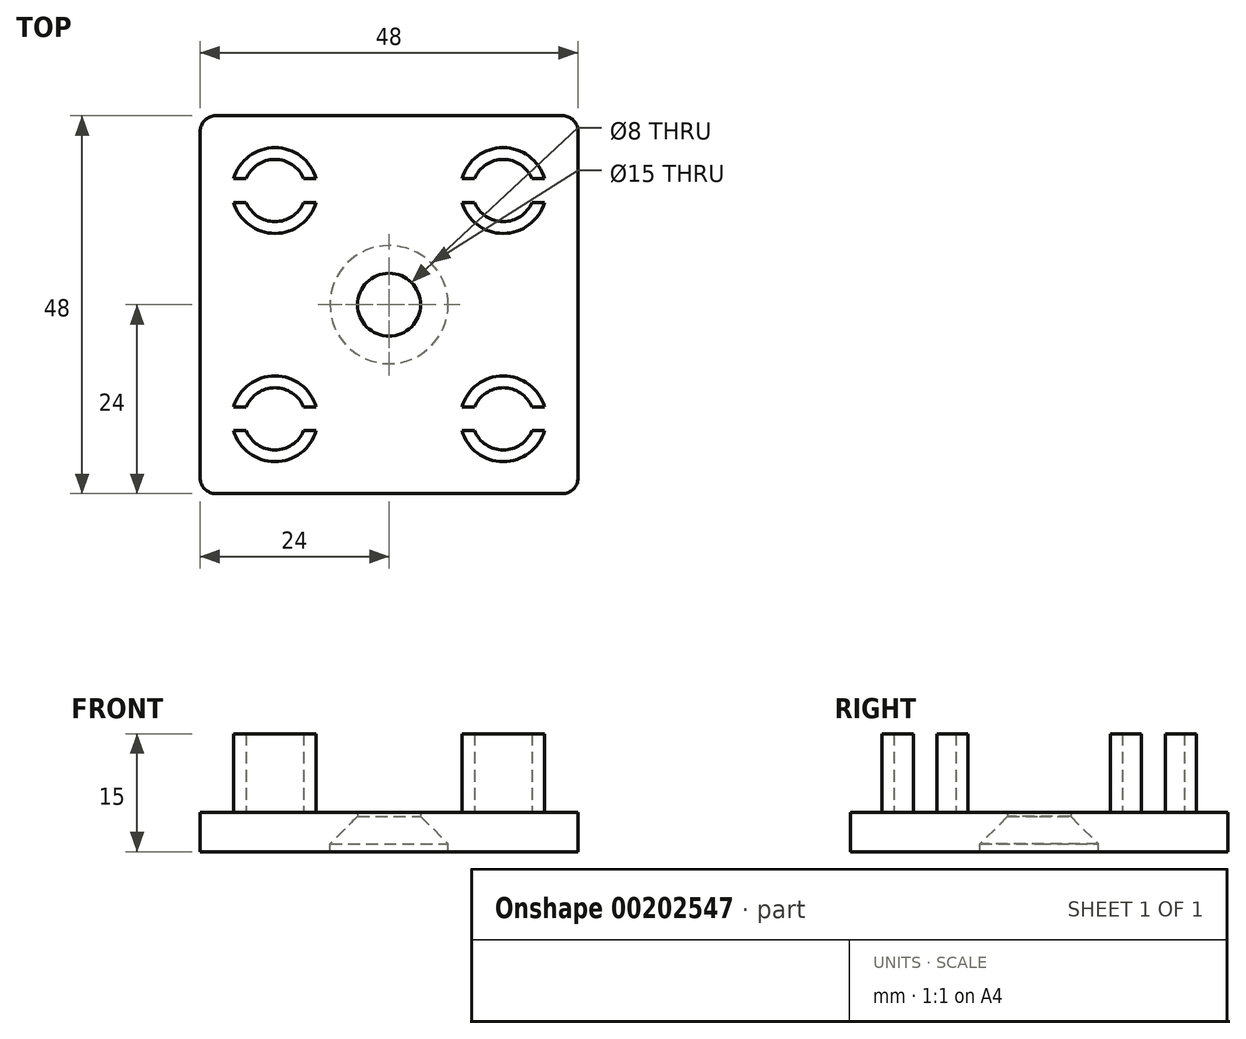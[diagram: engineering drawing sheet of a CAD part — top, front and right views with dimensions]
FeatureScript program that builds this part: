
annotation { "Feature Type Name" : "Feature", "Feature Type Description" : "" }
export const myFeature = defineFeature(function(context is Context, id is Id, definition is map)
    precondition{}
    {
        {
            var Q0;
            Q0=qCreatedBy(makeId("Top.planeOp"),FACE);
            var sketch = newSketch(context, id + "F0", { "sketchPlane" : qUnion([Q0])});
            skLineSegment(sketch, "E0.bottom", {"start": v(22, 24) * mm, "end": v(-22, 24) * mm});
            skLineSegment(sketch, "E0.top", {"start": v(22, -24) * mm, "end": v(-22, -24) * mm});
            skLineSegment(sketch, "E0.left", {"start": v(24, 22) * mm, "end": v(24, -22) * mm});
            skLineSegment(sketch, "E0.right", {"start": v(-24, 22) * mm, "end": v(-24, -22) * mm});
            skPoint(sketch, "E0.middle", {"position": v(0, 0) * mm});
            skPoint(sketch, "E1.visualSharp", {"position": v(-24, 24) * mm});
            skArc(sketch, "E1.filletArc", {"start": v(-22, 24) * mm, "mid": v(-23.41, 23.41) * mm, "end": v(-24, 22) * mm});
            skPoint(sketch, "E2.visualSharp", {"position": v(24, 24) * mm});
            skArc(sketch, "E2.filletArc", {"start": v(24, 22) * mm, "mid": v(23.41, 23.41) * mm, "end": v(22, 24) * mm});
            skPoint(sketch, "E3.visualSharp", {"position": v(24, -24) * mm});
            skArc(sketch, "E3.filletArc", {"start": v(22, -24) * mm, "mid": v(23.41, -23.41) * mm, "end": v(24, -22) * mm});
            skPoint(sketch, "E4.visualSharp", {"position": v(-24, -24) * mm});
            skArc(sketch, "E4.filletArc", {"start": v(-24, -22) * mm, "mid": v(-23.41, -23.41) * mm, "end": v(-22, -24) * mm});
            skLineSegment(sketch, "E5.0", {"start": v(18, 18) * mm, "end": v(-18, 18) * mm});
            skLineSegment(sketch, "E5.1", {"start": v(18, 18) * mm, "end": v(18, -18) * mm});
            skLineSegment(sketch, "E5.2", {"start": v(18, -18) * mm, "end": v(-18, -18) * mm});
            skLineSegment(sketch, "E5.3", {"start": v(-18, 18) * mm, "end": v(-18, -18) * mm});
            skSolve(sketch);
        }
        {
            var Q0;
            Q0=makeQuery(id+"F0.imprint","IMPRINT",FACE,{"disambiguationData":[TD([[makeQuery(id+"F0.imprint","IMPRINT",EDGE,{"derivedFrom":sQuery(id+"F0.wireOp",EDGE,"E0.bottom")}),1.0]])]});
            var Q1;
            Q1=makeQuery(id+"F0.imprint","IMPRINT",FACE,{"disambiguationData":[TD([[makeQuery(id+"F0.imprint","IMPRINT",EDGE,{"derivedFrom":sQuery(id+"F0.wireOp",EDGE,"E5.0")}),1.0]])]});
            extrude(context, id + "F1", {"entities" : qUnion([Q0, Q1]), "oppositeDirection" : true, "depth" : 4 * mm});
        }
        {
            var Q0;
            Q0=makeQuery(id+"F1.opExtrude","CAP_FACE",FACE,{"disambiguationData":[OSD([sQuery(id+"F0.wireOp",EDGE,"E0.bottom"),sQuery(id+"F0.wireOp",EDGE,"E0.top"),sQuery(id+"F0.wireOp",EDGE,"E0.left"),sQuery(id+"F0.wireOp",EDGE,"E0.right"),sQuery(id+"F0.wireOp",EDGE,"E1.filletArc"),sQuery(id+"F0.wireOp",EDGE,"E2.filletArc"),sQuery(id+"F0.wireOp",EDGE,"E3.filletArc"),sQuery(id+"F0.wireOp",EDGE,"E4.filletArc")])],"isStart":true});
            var sketch = newSketch(context, id + "F2", { "sketchPlane" : qUnion([Q0])});
            skLineSegment(sketch, "E6.0", {"start": v(20, 20) * mm, "end": v(-20, 20) * mm});
            skLineSegment(sketch, "E6.1", {"start": v(20, 20) * mm, "end": v(20, -20) * mm});
            skLineSegment(sketch, "E6.2", {"start": v(20, -20) * mm, "end": v(-20, -20) * mm});
            skLineSegment(sketch, "E6.3", {"start": v(-20, 20) * mm, "end": v(-20, -20) * mm});
            skCircle(sketch, "E7", {"center": v(0, 0) * mm, "radius": 3.75 * mm});
            skLineSegment(sketch, "E8.bottom", {"start": v(-20, 20) * mm, "end": v(-9, 20) * mm});
            skLineSegment(sketch, "E8.top", {"start": v(-20, 9) * mm, "end": v(-9, 9) * mm});
            skLineSegment(sketch, "E8.left", {"start": v(-20, 20) * mm, "end": v(-20, 9) * mm});
            skLineSegment(sketch, "E8.right", {"start": v(-9, 20) * mm, "end": v(-9, 9) * mm});
            skLineSegment(sketch, "E9.bottom", {"start": v(20, 20) * mm, "end": v(9, 20) * mm});
            skLineSegment(sketch, "E9.top", {"start": v(20, 9) * mm, "end": v(9, 9) * mm});
            skLineSegment(sketch, "E9.left", {"start": v(20, 20) * mm, "end": v(20, 9) * mm});
            skLineSegment(sketch, "E9.right", {"start": v(9, 20) * mm, "end": v(9, 9) * mm});
            skLineSegment(sketch, "E10.bottom", {"start": v(20, -20) * mm, "end": v(9, -20) * mm});
            skLineSegment(sketch, "E10.top", {"start": v(20, -9) * mm, "end": v(9, -9) * mm});
            skLineSegment(sketch, "E10.left", {"start": v(20, -20) * mm, "end": v(20, -9) * mm});
            skLineSegment(sketch, "E10.right", {"start": v(9, -20) * mm, "end": v(9, -9) * mm});
            skLineSegment(sketch, "E11.bottom", {"start": v(-20, -20) * mm, "end": v(-9, -20) * mm});
            skLineSegment(sketch, "E11.top", {"start": v(-20, -9) * mm, "end": v(-9, -9) * mm});
            skLineSegment(sketch, "E11.left", {"start": v(-20, -20) * mm, "end": v(-20, -9) * mm});
            skLineSegment(sketch, "E11.right", {"start": v(-9, -20) * mm, "end": v(-9, -9) * mm});
            skCircle(sketch, "E12", {"center": v(14.5, 14.5) * mm, "radius": 5.45 * mm});
            skPoint(sketch, "E12.centerSnap0", {"position": v(20, 14.5) * mm});
            skPoint(sketch, "E12.centerSnap1", {"position": v(14.5, 20) * mm});
            skCircle(sketch, "E13", {"center": v(-14.5, 14.5) * mm, "radius": 5.45 * mm});
            skPoint(sketch, "E13.centerSnap0", {"position": v(-14.5, 20) * mm});
            skPoint(sketch, "E13.centerSnap1", {"position": v(-9, 14.5) * mm});
            skCircle(sketch, "E14", {"center": v(-14.5, -14.5) * mm, "radius": 5.45 * mm});
            skPoint(sketch, "E14.centerSnap0", {"position": v(-14.5, -9) * mm});
            skPoint(sketch, "E14.centerSnap1", {"position": v(-9, -14.5) * mm});
            skCircle(sketch, "E15", {"center": v(14.5, -14.5) * mm, "radius": 5.45 * mm});
            skPoint(sketch, "E15.centerSnap0", {"position": v(14.5, -9) * mm});
            skPoint(sketch, "E15.centerSnap1", {"position": v(20, -14.5) * mm});
            skCircle(sketch, "E16", {"center": v(14.5, 14.5) * mm, "radius": 3.95 * mm});
            skCircle(sketch, "E17", {"center": v(14.5, -14.5) * mm, "radius": 3.95 * mm});
            skCircle(sketch, "E18", {"center": v(-14.5, -14.5) * mm, "radius": 3.95 * mm});
            skCircle(sketch, "E19", {"center": v(-14.5, 14.5) * mm, "radius": 3.95 * mm});
            skLineSegment(sketch, "E20.bottom", {"start": v(-9, 16) * mm, "end": v(-20, 16) * mm});
            skLineSegment(sketch, "E20.top", {"start": v(-9, 13) * mm, "end": v(-20, 13) * mm});
            skLineSegment(sketch, "E20.left", {"start": v(-9, 16) * mm, "end": v(-9, 13) * mm});
            skLineSegment(sketch, "E20.right", {"start": v(-20, 16) * mm, "end": v(-20, 13) * mm});
            skLineSegment(sketch, "E21.bottom", {"start": v(9, 16) * mm, "end": v(20, 16) * mm});
            skLineSegment(sketch, "E21.top", {"start": v(9, 13) * mm, "end": v(20, 13) * mm});
            skLineSegment(sketch, "E21.left", {"start": v(9, 16) * mm, "end": v(9, 13) * mm});
            skLineSegment(sketch, "E21.right", {"start": v(20, 16) * mm, "end": v(20, 13) * mm});
            skLineSegment(sketch, "E22.bottom", {"start": v(9, -13) * mm, "end": v(20, -13) * mm});
            skLineSegment(sketch, "E22.top", {"start": v(9, -16) * mm, "end": v(20, -16) * mm});
            skLineSegment(sketch, "E22.left", {"start": v(9, -13) * mm, "end": v(9, -16) * mm});
            skLineSegment(sketch, "E22.right", {"start": v(20, -13) * mm, "end": v(20, -16) * mm});
            skLineSegment(sketch, "E23.bottom", {"start": v(-9, -13) * mm, "end": v(-20, -13) * mm});
            skLineSegment(sketch, "E23.top", {"start": v(-9, -16) * mm, "end": v(-20, -16) * mm});
            skLineSegment(sketch, "E23.left", {"start": v(-9, -13) * mm, "end": v(-9, -16) * mm});
            skLineSegment(sketch, "E23.right", {"start": v(-20, -13) * mm, "end": v(-20, -16) * mm});
            skSolve(sketch);
        }
        {
            var Q0;
            {var subQ0=sQuery(id+"F2.wireOp",EDGE,"E20.bottom");var subQ1=sQuery(id+"F2.wireOp",EDGE,"E13");var subQ2=makeQuery(id+"F2.imprint","INTERSECT",VERTEX,{"disambiguationData":[OD(0.0)],"derivedFrom":[subQ1,subQ0]});Q0=makeQuery(id+"F2.imprint","IMPRINT",FACE,{"disambiguationData":[TD([[makeQuery(id+"F2.imprint","IMPRINT",EDGE,{"disambiguationData":[TD([[subQ2,1.0]])],"derivedFrom":subQ1}),1.0]])]});}
            var Q1;
            {var subQ0=sQuery(id+"F2.wireOp",EDGE,"E20.top");var subQ1=sQuery(id+"F2.wireOp",EDGE,"E13");var subQ2=makeQuery(id+"F2.imprint","INTERSECT",VERTEX,{"disambiguationData":[OD(0.0)],"derivedFrom":[subQ1,subQ0]});Q1=makeQuery(id+"F2.imprint","IMPRINT",FACE,{"disambiguationData":[TD([[makeQuery(id+"F2.imprint","IMPRINT",EDGE,{"disambiguationData":[TD([[subQ2,-1.0]])],"derivedFrom":subQ1}),1.0]])]});}
            var Q2;
            {var subQ0=sQuery(id+"F2.wireOp",EDGE,"E21.bottom");var subQ1=sQuery(id+"F2.wireOp",EDGE,"E12");var subQ2=makeQuery(id+"F2.imprint","INTERSECT",VERTEX,{"disambiguationData":[OD(0.0)],"derivedFrom":[subQ1,subQ0]});Q2=makeQuery(id+"F2.imprint","IMPRINT",FACE,{"disambiguationData":[TD([[makeQuery(id+"F2.imprint","IMPRINT",EDGE,{"disambiguationData":[TD([[subQ2,1.0]])],"derivedFrom":subQ1}),1.0]])]});}
            var Q3;
            {var subQ0=sQuery(id+"F2.wireOp",EDGE,"E21.top");var subQ1=sQuery(id+"F2.wireOp",EDGE,"E12");var subQ2=makeQuery(id+"F2.imprint","INTERSECT",VERTEX,{"disambiguationData":[OD(0.0)],"derivedFrom":[subQ1,subQ0]});Q3=makeQuery(id+"F2.imprint","IMPRINT",FACE,{"disambiguationData":[TD([[makeQuery(id+"F2.imprint","IMPRINT",EDGE,{"disambiguationData":[TD([[subQ2,-1.0]])],"derivedFrom":subQ1}),1.0]])]});}
            var Q4;
            {var subQ0=sQuery(id+"F2.wireOp",EDGE,"E22.bottom");var subQ1=sQuery(id+"F2.wireOp",EDGE,"E15");var subQ2=makeQuery(id+"F2.imprint","INTERSECT",VERTEX,{"disambiguationData":[OD(0.0)],"derivedFrom":[subQ1,subQ0]});Q4=makeQuery(id+"F2.imprint","IMPRINT",FACE,{"disambiguationData":[TD([[makeQuery(id+"F2.imprint","IMPRINT",EDGE,{"disambiguationData":[TD([[subQ2,1.0]])],"derivedFrom":subQ1}),1.0]])]});}
            var Q5;
            {var subQ0=sQuery(id+"F2.wireOp",EDGE,"E22.top");var subQ1=sQuery(id+"F2.wireOp",EDGE,"E15");var subQ2=makeQuery(id+"F2.imprint","INTERSECT",VERTEX,{"disambiguationData":[OD(0.0)],"derivedFrom":[subQ1,subQ0]});Q5=makeQuery(id+"F2.imprint","IMPRINT",FACE,{"disambiguationData":[TD([[makeQuery(id+"F2.imprint","IMPRINT",EDGE,{"disambiguationData":[TD([[subQ2,-1.0]])],"derivedFrom":subQ1}),1.0]])]});}
            var Q6;
            {var subQ0=sQuery(id+"F2.wireOp",EDGE,"E23.top");var subQ1=sQuery(id+"F2.wireOp",EDGE,"E14");var subQ2=makeQuery(id+"F2.imprint","INTERSECT",VERTEX,{"disambiguationData":[OD(0.0)],"derivedFrom":[subQ1,subQ0]});Q6=makeQuery(id+"F2.imprint","IMPRINT",FACE,{"disambiguationData":[TD([[makeQuery(id+"F2.imprint","IMPRINT",EDGE,{"disambiguationData":[TD([[subQ2,-1.0]])],"derivedFrom":subQ1}),1.0]])]});}
            var Q7;
            {var subQ0=sQuery(id+"F2.wireOp",EDGE,"E23.bottom");var subQ1=sQuery(id+"F2.wireOp",EDGE,"E14");var subQ2=makeQuery(id+"F2.imprint","INTERSECT",VERTEX,{"disambiguationData":[OD(0.0)],"derivedFrom":[subQ1,subQ0]});Q7=makeQuery(id+"F2.imprint","IMPRINT",FACE,{"disambiguationData":[TD([[makeQuery(id+"F2.imprint","IMPRINT",EDGE,{"disambiguationData":[TD([[subQ2,1.0]])],"derivedFrom":subQ1}),1.0]])]});}
            extrude(context, id + "F3", {"entities" : qUnion([Q0, Q1, Q2, Q3, Q4, Q5, Q6, Q7]), "operationType" : NewBodyOperationType.ADD, "depth" : 10 * mm});
        }
        {
            var Q0;
            Q0=makeQuery(id+"F1.opExtrude","CAP_FACE",FACE,{"disambiguationData":[OSD([sQuery(id+"F0.wireOp",EDGE,"E0.bottom"),sQuery(id+"F0.wireOp",EDGE,"E0.top"),sQuery(id+"F0.wireOp",EDGE,"E0.left"),sQuery(id+"F0.wireOp",EDGE,"E0.right"),sQuery(id+"F0.wireOp",EDGE,"E1.filletArc"),sQuery(id+"F0.wireOp",EDGE,"E2.filletArc"),sQuery(id+"F0.wireOp",EDGE,"E3.filletArc"),sQuery(id+"F0.wireOp",EDGE,"E4.filletArc")])],"isStart":false});
            var sketch = newSketch(context, id + "F4", { "sketchPlane" : qUnion([Q0])});
            skCircle(sketch, "E24", {"center": v(0, 0) * mm, "radius": 5.32 * mm});
            skSolve(sketch);
        }
        {
            var Q0;
            Q0=sQuery(id+"F4.wireOp",VERTEX,"E24.center");
            var Q1;
            Q1=makeQuery(id+"F1.opExtrude","SWEPT_BODY",BODY,{"disambiguationData":[OSD([sQuery(id+"F0.wireOp",EDGE,"E0.bottom"),sQuery(id+"F0.wireOp",EDGE,"E0.top"),sQuery(id+"F0.wireOp",EDGE,"E0.left"),sQuery(id+"F0.wireOp",EDGE,"E0.right"),sQuery(id+"F0.wireOp",EDGE,"E1.filletArc"),sQuery(id+"F0.wireOp",EDGE,"E2.filletArc"),sQuery(id+"F0.wireOp",EDGE,"E3.filletArc"),sQuery(id+"F0.wireOp",EDGE,"E4.filletArc")])]});
            hole(context, id + "F5", {"style" : HoleStyle.C_SINK, "endStyle" : HoleEndStyle.THROUGH, "holeDiameter" : 8 * mm, "cSinkDiameter" : 15 * mm, "cSinkAngle" : 90 * degree, "locations" : qUnion([Q0]), "scope" : qUnion([Q1]), "isTappedThrough" : true});
        }
        {
            var Q0;
            Q0=makeQuery(id+"F1.opExtrude","CAP_FACE",FACE,{"disambiguationData":[OSD([sQuery(id+"F0.wireOp",EDGE,"E0.bottom"),sQuery(id+"F0.wireOp",EDGE,"E0.top"),sQuery(id+"F0.wireOp",EDGE,"E0.left"),sQuery(id+"F0.wireOp",EDGE,"E0.right"),sQuery(id+"F0.wireOp",EDGE,"E1.filletArc"),sQuery(id+"F0.wireOp",EDGE,"E2.filletArc"),sQuery(id+"F0.wireOp",EDGE,"E3.filletArc"),sQuery(id+"F0.wireOp",EDGE,"E4.filletArc")])],"isStart":false});
            extrude(context, id + "F6", {"entities" : qUnion([Q0]), "operationType" : NewBodyOperationType.ADD, "depth" : 1 * mm});
        }
    });
